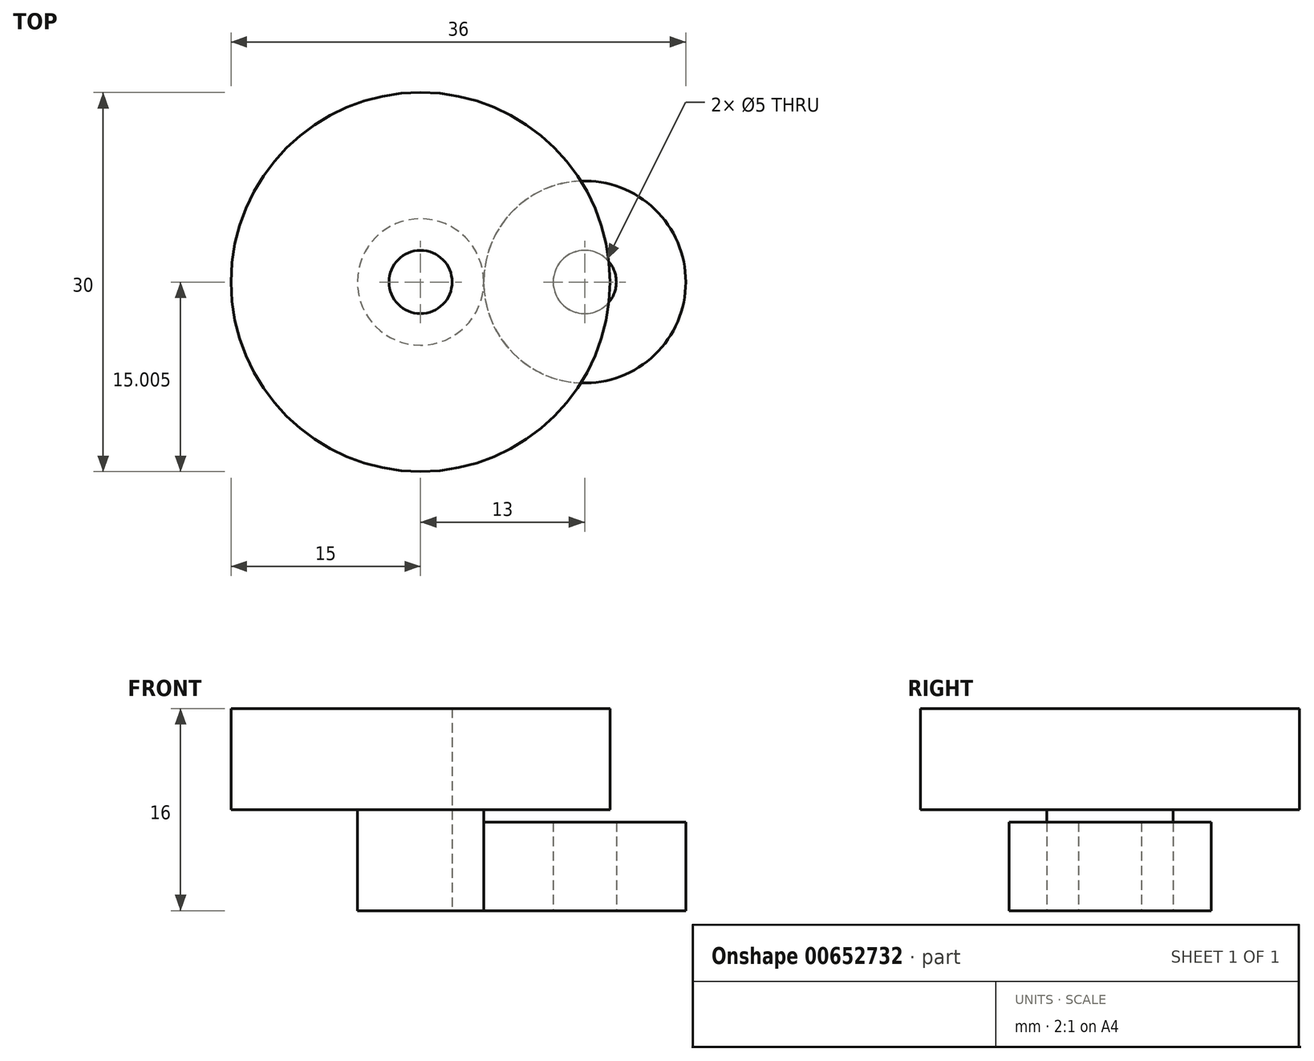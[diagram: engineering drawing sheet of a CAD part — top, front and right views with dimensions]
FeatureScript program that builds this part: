
annotation { "Feature Type Name" : "Feature", "Feature Type Description" : "" }
export const myFeature = defineFeature(function(context is Context, id is Id, definition is map)
    precondition{}
    {
        {
            var Q0;
            Q0=qCreatedBy(makeId("Top.planeOp"),FACE);
            var sketch = newSketch(context, id + "F0", { "sketchPlane" : qUnion([Q0])});
            skLineSegment(sketch, "E0.bottom", {"start": v(-6, 50) * mm, "end": v(6, 50) * mm});
            skCircle(sketch, "E1", {"center": v(-21, -35.06) * mm, "radius": 15 * mm});
            skCircle(sketch, "E2", {"center": v(-21, -35.06) * mm, "radius": 5 * mm});
            skCircle(sketch, "E3", {"center": v(-8, -35.06) * mm, "radius": 8 * mm});
            skCircle(sketch, "E4", {"center": v(-8, -35.06) * mm, "radius": 2.5 * mm});
            skCircle(sketch, "E5", {"center": v(-21, -35.06) * mm, "radius": 2.5 * mm});
            skSolve(sketch);
        }
        {
            var Q0;
            Q0=makeQuery(id+"F0.imprint","IMPRINT",FACE,{"disambiguationData":[TD([[makeQuery(id+"F0.imprint","IMPRINT",EDGE,{"derivedFrom":sQuery(id+"F0.wireOp",EDGE,"E2")}),1.0]])]});
            extrude(context, id + "F1", {"entities" : qUnion([Q0]), "depth" : 8 * mm, "offsetDistance" : 25 * mm});
        }
        {
            var Q0;
            Q0=makeQuery(id+"F1.opExtrude","CAP_FACE",FACE,{"disambiguationData":[OSD([sQuery(id+"F0.wireOp",EDGE,"E2")])],"isStart":false});
            var sketch = newSketch(context, id + "F2", { "sketchPlane" : qUnion([Q0])});
            skCircle(sketch, "E6.0", {"center": v(-21, -35.06) * mm, "radius": 15 * mm});
            skSolve(sketch);
        }
        {
            var Q0;
            Q0=makeQuery(id+"F2.imprint","IMPRINT",FACE,{"disambiguationData":[TD([[makeQuery(id+"F2.imprint","IMPRINT",EDGE,{"derivedFrom":makeQuery(id+"F1.opExtrude","CAP_EDGE",EDGE,{"disambiguationData":[OSD([sQuery(id+"F0.wireOp",EDGE,"E2")])],"isStart":false})}),1.0]])]});
            var Q1;
            Q1=makeQuery(id+"F2.imprint","IMPRINT",FACE,{"disambiguationData":[TD([[makeQuery(id+"F2.imprint","IMPRINT",EDGE,{"derivedFrom":sQuery(id+"F2.wireOp",EDGE,"E6.0")}),1.0]])]});
            extrude(context, id + "F3", {"entities" : qUnion([Q0, Q1]), "operationType" : NewBodyOperationType.ADD, "depth" : 8 * mm, "offsetDistance" : 25 * mm});
        }
        {
            var Q0;
            {var subQ0=sQuery(id+"F0.wireOp",EDGE,"lUt5lqVD-F3Tl-bQ9z-GRec-awnmSR3xUwSJ");var subQ1=sQuery(id+"F0.wireOp",EDGE,"E1");var subQ2=makeQuery(id+"F0.imprint","INTERSECT",VERTEX,{"disambiguationData":[OD(0.0)],"derivedFrom":[subQ1,subQ0]});Q0=makeQuery(id+"F0.imprint","IMPRINT",FACE,{"disambiguationData":[TD([[makeQuery(id+"F0.imprint","IMPRINT",EDGE,{"disambiguationData":[TD([[subQ2,1.0]])],"derivedFrom":subQ1}),1.0]])]});}
            var Q1;
            {var subQ0=sQuery(id+"F0.wireOp",EDGE,"lUt5lqVD-F3Tl-bQ9z-GRec-awnmSR3xUwSJ");var subQ1=sQuery(id+"F0.wireOp",EDGE,"E1");var subQ2=makeQuery(id+"F0.imprint","INTERSECT",VERTEX,{"disambiguationData":[OD(0.0)],"derivedFrom":[subQ1,subQ0]});Q1=makeQuery(id+"F0.imprint","IMPRINT",FACE,{"disambiguationData":[TD([[makeQuery(id+"F0.imprint","IMPRINT",EDGE,{"disambiguationData":[TD([[subQ2,1.0]])],"derivedFrom":subQ1}),-1.0]])]});}
            var Q2;
            {var subQ0=sQuery(id+"F0.wireOp",EDGE,"E3");var subQ1=sQuery(id+"F0.wireOp",EDGE,"E1");var subQ6=makeQuery(id+"F0.imprint","INTERSECT",VERTEX,{"disambiguationData":[OD(0.0)],"derivedFrom":[subQ1,subQ0]});Q2=makeQuery(id+"F0.imprint","IMPRINT",FACE,{"disambiguationData":[TD([[makeQuery(id+"F0.imprint","IMPRINT",EDGE,{"disambiguationData":[TD([[subQ6,1.0]])],"derivedFrom":subQ1}),1.0]])]});}
            var Q3;
            {var subQ0=sQuery(id+"F0.wireOp",EDGE,"E3");var subQ1=sQuery(id+"F0.wireOp",EDGE,"E1");var subQ2=makeQuery(id+"F0.imprint","INTERSECT",VERTEX,{"disambiguationData":[OD(0.0)],"derivedFrom":[subQ1,subQ0]});Q3=makeQuery(id+"F0.imprint","IMPRINT",FACE,{"disambiguationData":[TD([[makeQuery(id+"F0.imprint","IMPRINT",EDGE,{"disambiguationData":[TD([[subQ2,1.0]])],"derivedFrom":subQ1}),-1.0]])]});}
            extrude(context, id + "F4", {"entities" : qUnion([Q0, Q1, Q2, Q3]), "operationType" : NewBodyOperationType.ADD, "depth" : 7 * mm, "offsetDistance" : 25 * mm});
        }
    });
